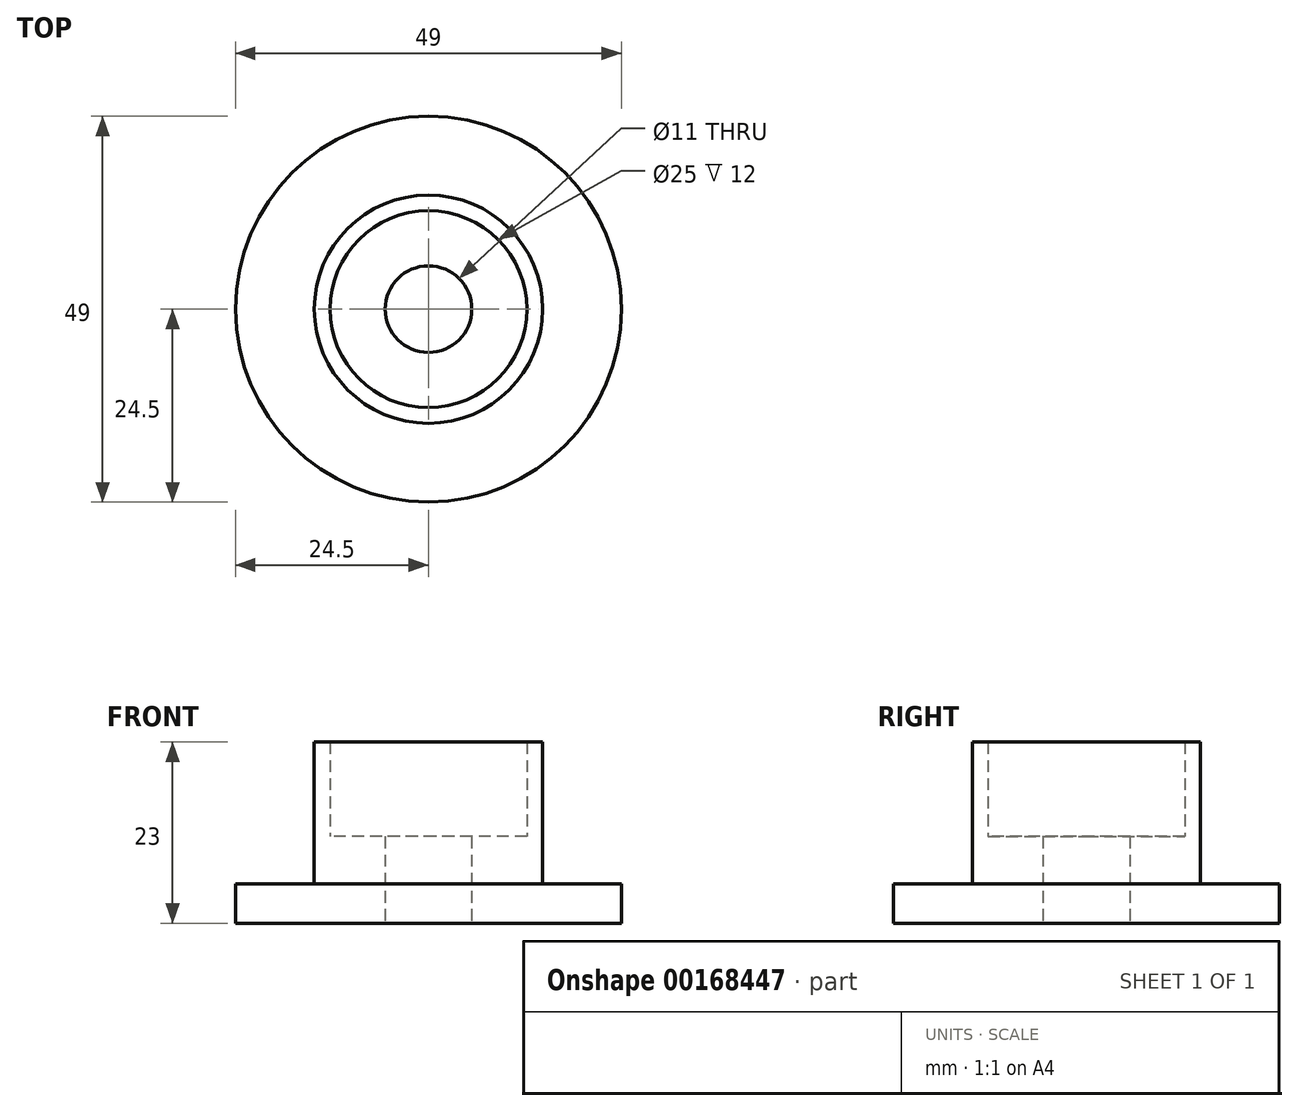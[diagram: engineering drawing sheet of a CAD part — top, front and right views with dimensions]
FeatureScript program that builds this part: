
annotation { "Feature Type Name" : "Feature", "Feature Type Description" : "" }
export const myFeature = defineFeature(function(context is Context, id is Id, definition is map)
    precondition{}
    {
        {
            var Q0;
            Q0=qCreatedBy(makeId("Top.planeOp"),FACE);
            var sketch = newSketch(context, id + "F0", { "sketchPlane" : qUnion([Q0])});
            skCircle(sketch, "E0", {"center": v(0, 0) * mm, "radius": 24.5 * mm});
            skCircle(sketch, "E1", {"center": v(0, 0) * mm, "radius": 5.5 * mm});
            skSolve(sketch);
        }
        {
            var Q0;
            Q0=makeQuery(id+"F0.imprint","IMPRINT",FACE,{"disambiguationData":[TD([[makeQuery(id+"F0.imprint","IMPRINT",EDGE,{"derivedFrom":sQuery(id+"F0.wireOp",EDGE,"E0")}),1.0]])]});
            extrude(context, id + "F1", {"entities" : qUnion([Q0]), "depth" : 5 * mm, "offsetDistance" : 25 * mm});
        }
        {
            var Q0;
            Q0=makeQuery(id+"F1.opExtrude","CAP_FACE",FACE,{"disambiguationData":[OSD([sQuery(id+"F0.wireOp",EDGE,"E0"),sQuery(id+"F0.wireOp",EDGE,"E1")])],"isStart":false});
            var sketch = newSketch(context, id + "F2", { "sketchPlane" : qUnion([Q0])});
            skCircle(sketch, "E2", {"center": v(0, 0) * mm, "radius": 14.5 * mm});
            skSolve(sketch);
        }
        {
            var Q0;
            Q0=makeQuery(id+"F2.imprint","IMPRINT",FACE,{"disambiguationData":[TD([[makeQuery(id+"F2.imprint","IMPRINT",EDGE,{"derivedFrom":sQuery(id+"F2.wireOp",EDGE,"E2")}),1.0]])]});
            extrude(context, id + "F3", {"entities" : qUnion([Q0]), "operationType" : NewBodyOperationType.ADD, "depth" : 6 * mm, "offsetDistance" : 25 * mm});
        }
        {
            var Q0;
            Q0=makeQuery(id+"F3.opExtrude","CAP_FACE",FACE,{"disambiguationData":[OSD([sQuery(id+"F0.wireOp",EDGE,"E1"),sQuery(id+"F2.wireOp",EDGE,"E2")])],"isStart":false});
            var sketch = newSketch(context, id + "F4", { "sketchPlane" : qUnion([Q0])});
            skCircle(sketch, "E3", {"center": v(0, 0) * mm, "radius": 12.5 * mm});
            skCircle(sketch, "E4", {"center": v(0, 0) * mm, "radius": 10 * mm});
            skSolve(sketch);
        }
        {
            var Q0;
            Q0=makeQuery(id+"F4.imprint","IMPRINT",FACE,{"disambiguationData":[TD([[makeQuery(id+"F4.imprint","IMPRINT",EDGE,{"derivedFrom":sQuery(id+"F4.wireOp",EDGE,"E3")}),-1.0]])]});
            var Q1;
            Q1=makeQuery(id+"F4.imprint","IMPRINT",FACE,{"disambiguationData":[TD([[makeQuery(id+"F4.imprint","IMPRINT",EDGE,{"derivedFrom":makeQuery(id+"F3.opExtrude","CAP_EDGE",EDGE,{"disambiguationData":[OSD([sQuery(id+"F2.wireOp",EDGE,"E2")])],"isStart":false})}),1.0]])]});
            extrude(context, id + "F5", {"entities" : qUnion([Q0, Q1]), "operationType" : NewBodyOperationType.ADD, "depth" : 12 * mm, "offsetDistance" : 25 * mm});
        }
    });
